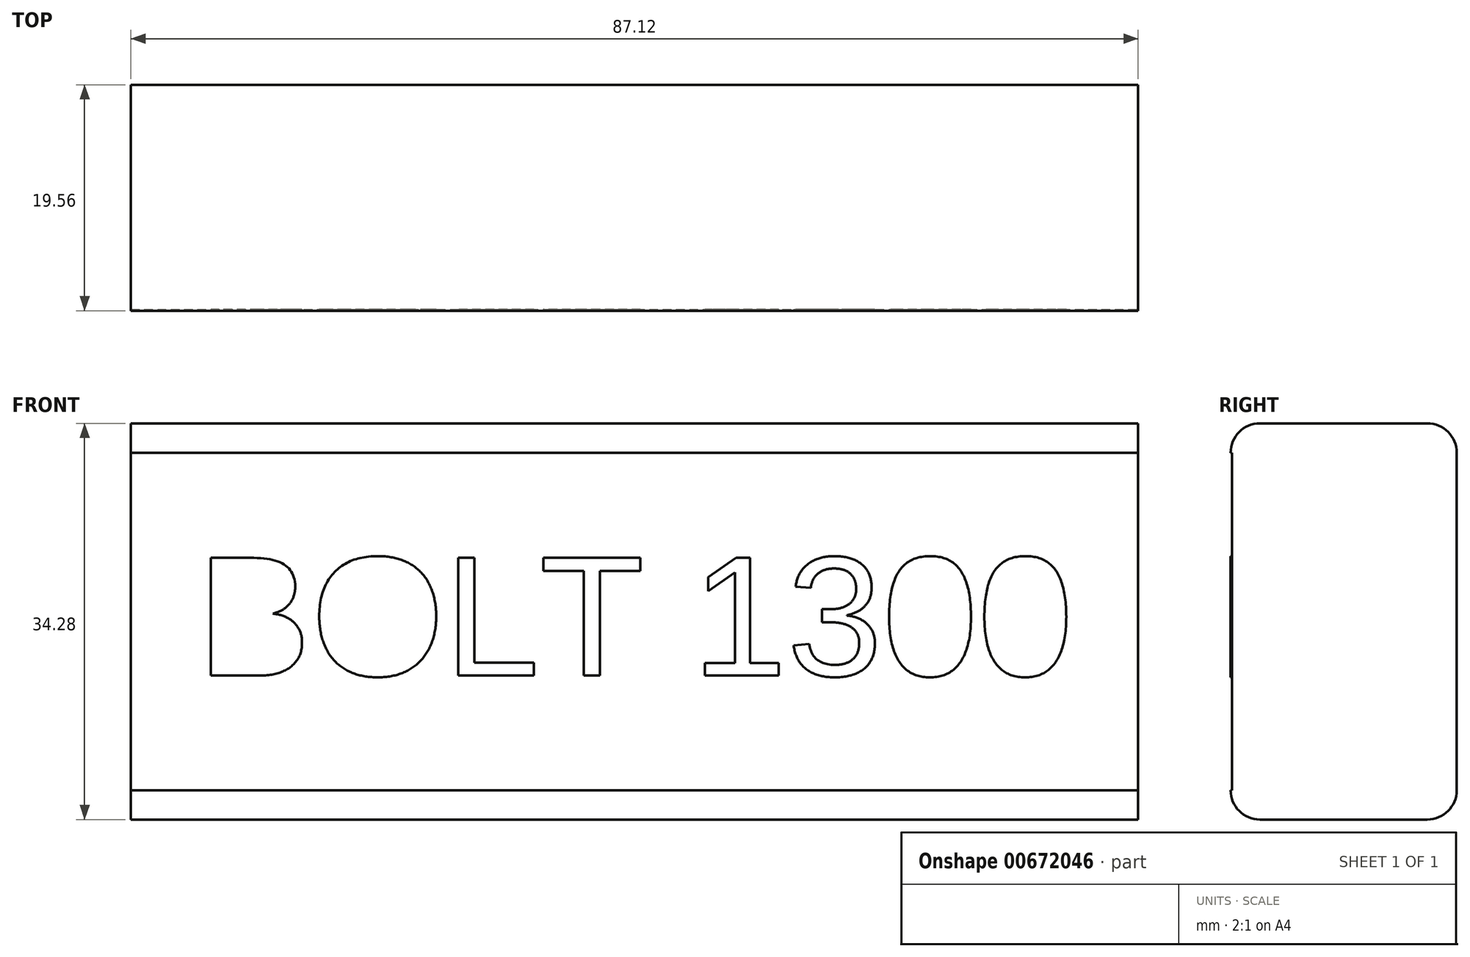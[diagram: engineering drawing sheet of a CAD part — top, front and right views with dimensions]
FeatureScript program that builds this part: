
annotation { "Feature Type Name" : "Feature", "Feature Type Description" : "" }
export const myFeature = defineFeature(function(context is Context, id is Id, definition is map)
    precondition{}
    {
        {
            var Q0;
            Q0=qCreatedBy(makeId("Front.planeOp"),FACE);
            var sketch = newSketch(context, id + "F0", { "sketchPlane" : qUnion([Q0])});
            skLineSegment(sketch, "E0.bottom", {"start": v(-43.56, 17.15) * mm, "end": v(43.56, 17.15) * mm});
            skLineSegment(sketch, "E0.top", {"start": v(-43.56, -17.14) * mm, "end": v(43.56, -17.14) * mm});
            skLineSegment(sketch, "E0.left", {"start": v(-43.56, 17.15) * mm, "end": v(-43.56, -17.15) * mm});
            skLineSegment(sketch, "E0.right", {"start": v(43.56, 17.15) * mm, "end": v(43.56, -17.14) * mm});
            skPoint(sketch, "E0.middle", {"position": v(0, 0) * mm});
            skSolve(sketch);
        }
        {
            var Q0;
            Q0=qSketchRegion(id+"F0",true);
            extrude(context, id + "F1", {"entities" : qUnion([Q0]), "endBound" : BoundingType.SYMMETRIC, "depth" : 19.56 * mm, "offsetDistance" : 25.4 * mm});
        }
        {
            var Q0;
            Q0=makeQuery(id+"F1.opExtrude","CAP_EDGE",EDGE,{"disambiguationData":[OSD([sQuery(id+"F0.wireOp",EDGE,"E0.bottom")])],"isStart":true});
            var Q1;
            Q1=makeQuery(id+"F1.opExtrude","CAP_EDGE",EDGE,{"disambiguationData":[OSD([sQuery(id+"F0.wireOp",EDGE,"E0.top")])],"isStart":true});
            var Q2;
            Q2=makeQuery(id+"F1.opExtrude","CAP_EDGE",EDGE,{"disambiguationData":[OSD([sQuery(id+"F0.wireOp",EDGE,"E0.bottom")])],"isStart":false});
            var Q3;
            Q3=makeQuery(id+"F1.opExtrude","CAP_EDGE",EDGE,{"disambiguationData":[OSD([sQuery(id+"F0.wireOp",EDGE,"E0.top")])],"isStart":false});
            fillet(context, id + "F2", {"entities" : qUnion([Q0, Q1, Q2, Q3]), "radius" : 2.54 * mm, "tangentPropagation" : true, "allowEdgeOverflow" : false});
        }
        {
            var Q0;
            Q0=makeQuery(id+"F1.opExtrude","CAP_FACE",FACE,{"disambiguationData":[OSD([sQuery(id+"F0.wireOp",EDGE,"E0.bottom"),sQuery(id+"F0.wireOp",EDGE,"E0.top"),sQuery(id+"F0.wireOp",EDGE,"E0.left"),sQuery(id+"F0.wireOp",EDGE,"E0.right")])],"isStart":false});
            var sketch = newSketch(context, id + "F3", { "sketchPlane" : qUnion([Q0])});
            skText(sketch, "E1", { "text": "BOLT 1300", "fontName": "Arimo-Regular.ttf"});
            const initialGuessF3  = {"E1": [-0.03786, -0.00469, 1, 0, 0.01067]};
            skSetInitialGuess(sketch, initialGuessF3);
            skSolve(sketch);
        }
        {
            var Q0;
            Q0=makeQuery(id+"F3.imprint","IMPRINT",FACE,{"disambiguationData":[TD([[makeQuery(id+"F3.imprint","IMPRINT",EDGE,{"derivedFrom":sQuery(id+"F3.wireOp",EDGE,"E1.sketch_text.stroke-0")}),1.0]])]});
            extrude(context, id + "F4", {"entities" : qUnion([Q0]), "operationType" : NewBodyOperationType.REMOVE, "oppositeDirection" : true, "depth" : 0.13 * mm, "offsetDistance" : 25.4 * mm});
        }
    });
